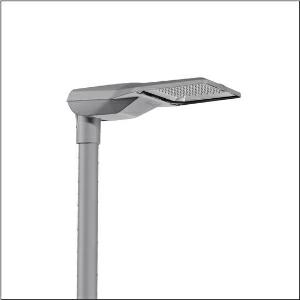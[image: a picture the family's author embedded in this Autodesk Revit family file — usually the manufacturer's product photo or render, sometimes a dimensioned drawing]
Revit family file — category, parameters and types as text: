
# Revit family: streetlight_sl_21_iq_midi___stw1_0a_5xe3e41d08mb_aeb4
name_source: partatom
category: Lighting Fixtures
units: mm (PartAtom-declared; Revit-internal decimal feet)

## family parameters
Cut with Voids When Loaded = No
Host = Face
Light Source = No
Part Type = Normal
Room Calculation Point = No
Round Connector Dimension = Use Diameter
Shared = No

## types (1)
- --- (1 x LED, 20360 lm, 146.7 W, 4000K)
    Apparent Load = 147 VA
    CIE Flux Codes = 38 75 98 100 100
    Color Rendering = 70
    Color Temperature = 4000K
    Default Elevation = 1800 mm
    Description = Streetlight SL 21 iQ midi, mast luminaire, primary light control with lens, of PMMA, primary optical cover: cover, of toughened safety glass, transparent, light distribution: STW1.0a, light emission: direct distribution, primary light characteristic: asymmetric, installation type: post-top, side-entry, LED, High Power LED, rated luminous flux: 20.360lm, luminous efficacy: 139lm/W, light colour: 740, colour temperature: 4000K, control: Auto-Match, Temp-Guard, Lumen-Switch, Night-Set, Smart-Wire, Light-Fading, Desk-Remote (wireless, voltage-free reading and setting of iQ features in the workshop via application-optimized NFC function/RFID function), optimised constant luminous flux control (CLO 2.0), presetting dimming linear, mains connection: 230..240V, AC, 50/60Hz, start of lifetime: 147W, end of service life: 161W, reduction: 62W, luminaire housing, of diecast aluminium, powder-coated, Siteco® metallic grey (DB 702S), corrosivity category C5 mid according to DIN EN ISO 12944, please order mast flange separately, inclination adjustable: 0°, 5°, 10°, 15°, sealing non-destructively replaceable, multi-level sealing system, length: 644mm, width: 335mm, height: 110mm, mast flange for spigot size: 42mm (side-entry): 5XC10008XM4, 60/48mm (side-entry/post-top): 5XC10108XM2, 76/60mm (side-entry/post-top): 5XC10108XM1, protection rating (complete): IP66, insulation class (complete): insulation class II (safety insulation), certification: CE, ENEC, ENEC+, VDE, impact resistance: IK09, permissible operating ambient temperature for outdoor applications: -40..+50°C, standard-compliant lighting for roads and squares, packaging unit: 1 piece

Light Distribution: STW1.0a
    Height = 111 mm
    Lamp = 1 x LED
    Lamp Light Flux = 20360 lm
    Lamp Power = 146.7 W
    Lamp count = 1
    Length = 644 mm
    Luminous efficacy = 139 lm/W
    Manufacturer = Siteco
    ModVariant = No
    Model = 5XE3E41D08MB
    Number of Poles = 1
    OnlyDefault = Yes
    Power Factor = 1
    Product Name = Streetlight SL 21 iQ midi | STW1.0a
    Product group = mast luminaire | pylon top
    ProductGroupID = 6100
    Protection Class = Protection class II
    Protection Degree = IP 66
    RLX_Detail_Level = 1
    RLX_Emergency_Light_Flux = 0 lm
    RLX_Emergency_Type = 0
    RLX_Emergency_Type_DB = No
    RlxData = <blob elided: 90805 chars, md5=913d277d>
    Socket = socket
    Standby Power = 0 W
    System Light Flux = 20360 lm
    System Power = 147 W
    Type Comments = factory setting: luminous flux: 100 % | dim-lin: 254 | 753 mA
    Type Image = l_1004298.jpg
    URL = http://relux.com
    VarID = @adj_140119
    Voltage = 0 V
    Weight = 0.00 kg
    Width = 336 mm

## geometry (parser evidence)
native form markers: Blend x4, Sweep x11
no freeform markers — native parametric forms only
